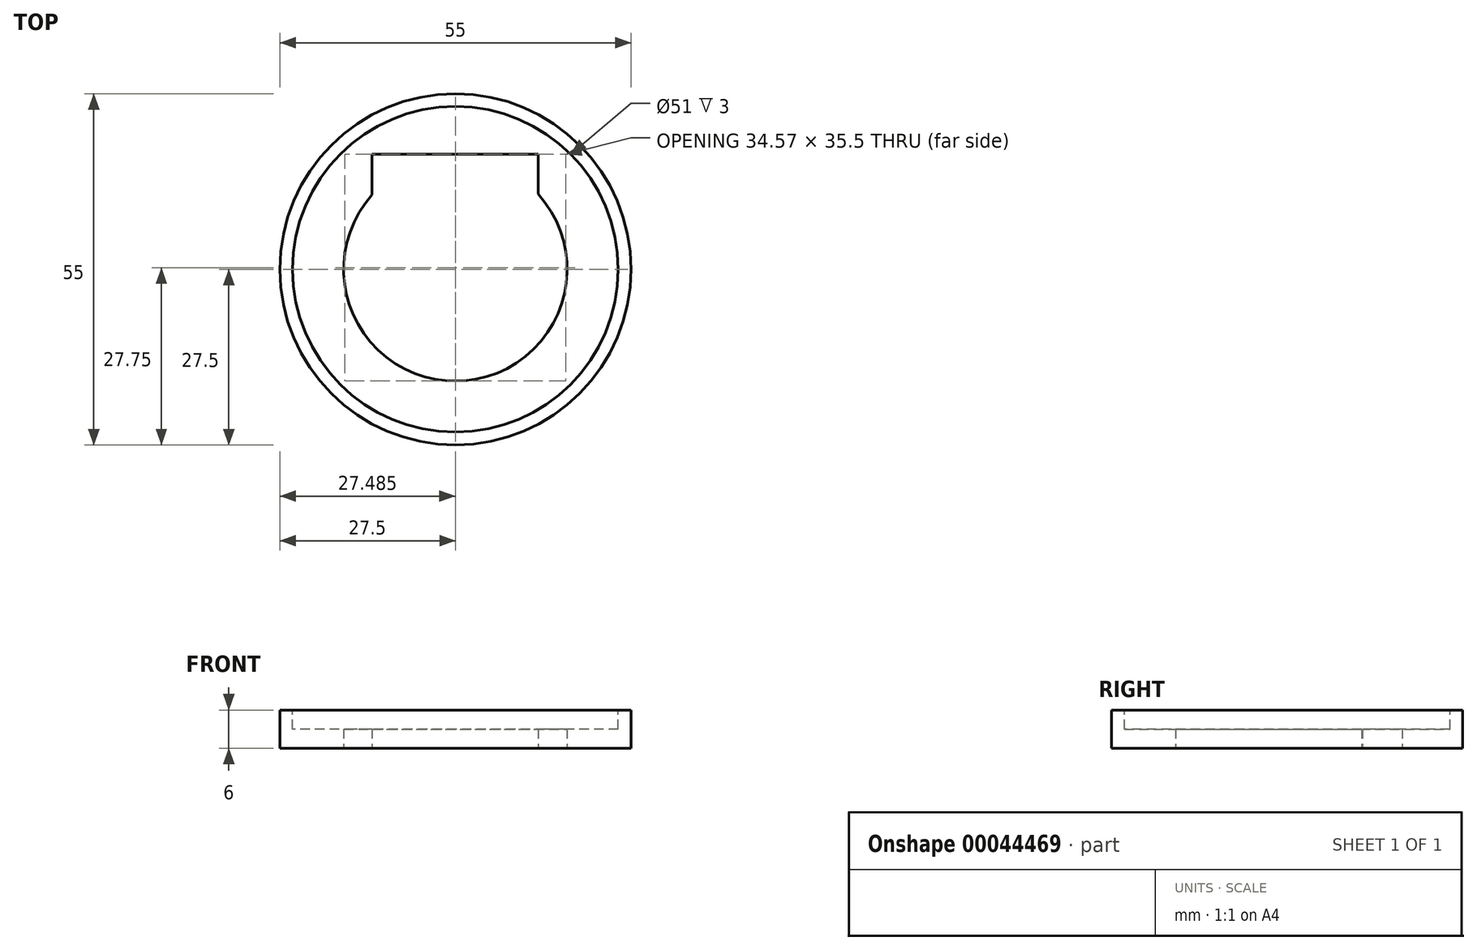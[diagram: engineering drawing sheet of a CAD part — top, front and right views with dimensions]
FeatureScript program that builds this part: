
annotation { "Feature Type Name" : "Feature", "Feature Type Description" : "" }
export const myFeature = defineFeature(function(context is Context, id is Id, definition is map)
    precondition{}
    {
        {
            var Q0;
            Q0=qCreatedBy(makeId("Top.planeOp"),FACE);
            var sketch = newSketch(context, id + "F0", { "sketchPlane" : qUnion([Q0])});
            skCircle(sketch, "E0", {"center": v(0, 0) * mm, "radius": 17.5 * mm});
            skCircle(sketch, "E1", {"center": v(0, 0) * mm, "radius": 27.5 * mm});
            skSolve(sketch);
        }
        {
            var Q0;
            Q0 = qSketchRegion(id + "F0", true);
            var Q1;
            Q1=makeQuery(id+"F0.imprint","IMPRINT",FACE,{"disambiguationData":[TD([[makeQuery(id+"F0.imprint","IMPRINT",EDGE,{"derivedFrom":sQuery(id+"F0.wireOp",EDGE,"E0")}),-1.0]])]});
            extrude(context, id + "F1", {"entities" : qUnion([Q0, Q1]), "depth" : 6 * mm});
        }
        {
            var Q0;
            Q0=makeQuery(id+"F1.opExtrude","CAP_FACE",FACE,{"disambiguationData":[OSD([sQuery(id+"F0.wireOp",EDGE,"E0"),sQuery(id+"F0.wireOp",EDGE,"E1")])],"isStart":false});
            var sketch = newSketch(context, id + "F2", { "sketchPlane" : qUnion([Q0])});
            skCircle(sketch, "E2", {"center": v(0, 0) * mm, "radius": 25.5 * mm});
            skSolve(sketch);
        }
        {
            var Q0;
            Q0 = qSketchRegion(id + "F2", true);
            var Q1;
            Q1=makeQuery(id+"F2.imprint","IMPRINT",FACE,{"disambiguationData":[TD([[makeQuery(id+"F2.imprint","IMPRINT",EDGE,{"derivedFrom":sQuery(id+"F2.wireOp",EDGE,"E2")}),1.0]])]});
            extrude(context, id + "F3", {"entities" : qUnion([Q0, Q1]), "operationType" : NewBodyOperationType.REMOVE, "oppositeDirection" : true, "depth" : 3 * mm});
        }
        {
            var Q0;
            Q0=makeQuery(id+"F1.opExtrude","CAP_FACE",FACE,{"disambiguationData":[OSD([sQuery(id+"F0.wireOp",EDGE,"E0"),sQuery(id+"F0.wireOp",EDGE,"E1")])],"isStart":true});
            var sketch = newSketch(context, id + "F4", { "sketchPlane" : qUnion([Q0])});
            skLineSegment(sketch, "E3.bottom", {"start": v(12.94, 6) * mm, "end": v(-13.06, 6) * mm});
            skLineSegment(sketch, "E3.top", {"start": v(12.94, -18) * mm, "end": v(-13.06, -18) * mm});
            skLineSegment(sketch, "E3.left", {"start": v(12.94, 6) * mm, "end": v(12.94, -18) * mm});
            skLineSegment(sketch, "E3.right", {"start": v(-13.06, 6) * mm, "end": v(-13.06, -18) * mm});
            skSolve(sketch);
        }
        {
            var Q0;
            Q0 = qSketchRegion(id + "F4", true);
            extrude(context, id + "F5", {"entities" : qUnion([Q0]), "operationType" : NewBodyOperationType.REMOVE, "oppositeDirection" : true, "depth" : 25 * mm});
        }
    });
